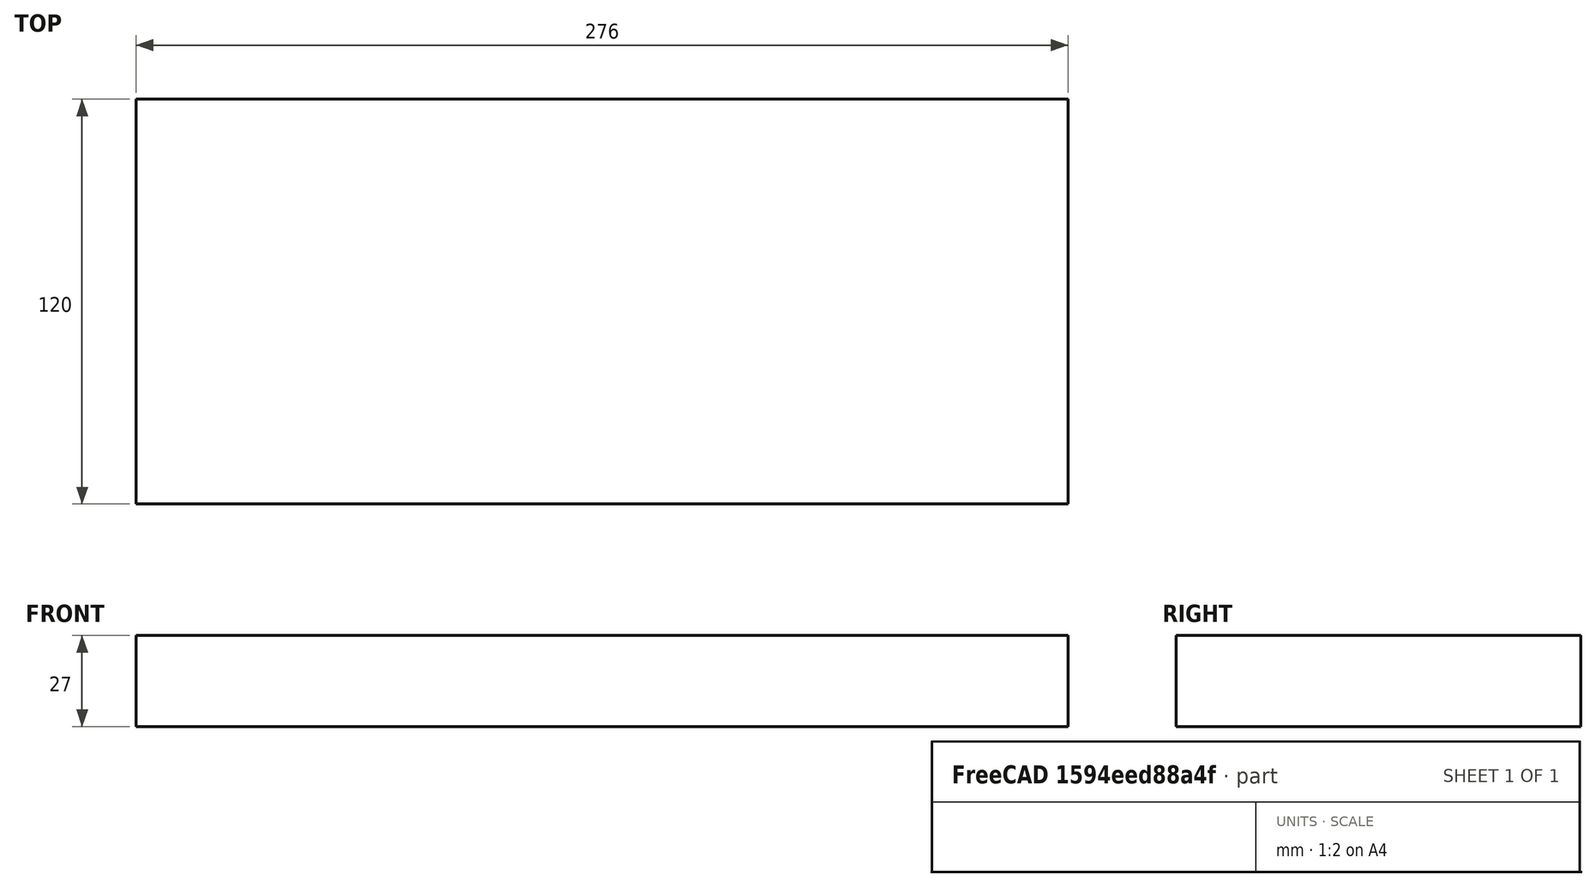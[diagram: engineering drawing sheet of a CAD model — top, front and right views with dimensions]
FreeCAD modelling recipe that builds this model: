
FCSTD DOCUMENT  (FreeCAD 0.21R33771 (Git))
Label: fan-board
License: All rights reserved
LicenseURL: http://en.wikipedia.org/wiki/All_rights_reserved
objects: Sketcher::SketchObject×1, PartDesign::Pad×1, PartDesign::Body×1
note: 4 computed .brp shape members not serialized (recipe doc carries the construction recipe); baked Part::Feature solids carry a one-line shape summary decoded from their .brp

FEATURE [Sketcher::SketchObject] Sketch
  FullyConstrained = true
  MapMode = 5
  Support = -> [XY_Plane]
  sketch-geometry (4):
    g0: LineSegment StartX=0 StartY=0 StartZ=0 EndX=276 EndY=0 EndZ=0
    g1: LineSegment StartX=276 StartY=0 StartZ=0 EndX=276 EndY=120 EndZ=0
    g2: LineSegment StartX=276 StartY=120 StartZ=0 EndX=0 EndY=120 EndZ=0
    g3: LineSegment StartX=0 StartY=120 StartZ=0 EndX=0 EndY=0 EndZ=0
  constraints (11):
    c: Coincident(g0,g1)
    c: Coincident(g1,g2)
    c: Coincident(g2,g3)
    c: Coincident(g3,g0)
    c: Horizontal(g0)
    c: Horizontal(g2)
    c: Vertical(g1)
    c: Vertical(g3)
    c: Coincident(g0,g-1)
    c: DistanceY(g3,g3) = 120
    c: DistanceX(g0,g0) = 276
FEATURE [PartDesign::Pad] Pad
  Direction = (0,0,1)
  Length = 27
  Length2 = 10
  Profile = -> Sketch
  ReferenceAxis = -> Sketch [N_Axis]
  Type = 0
FEATURE [PartDesign::Body] Body
  Group = -> [Sketch,Pad]
  Origin = -> Origin
  Tip = -> Pad
